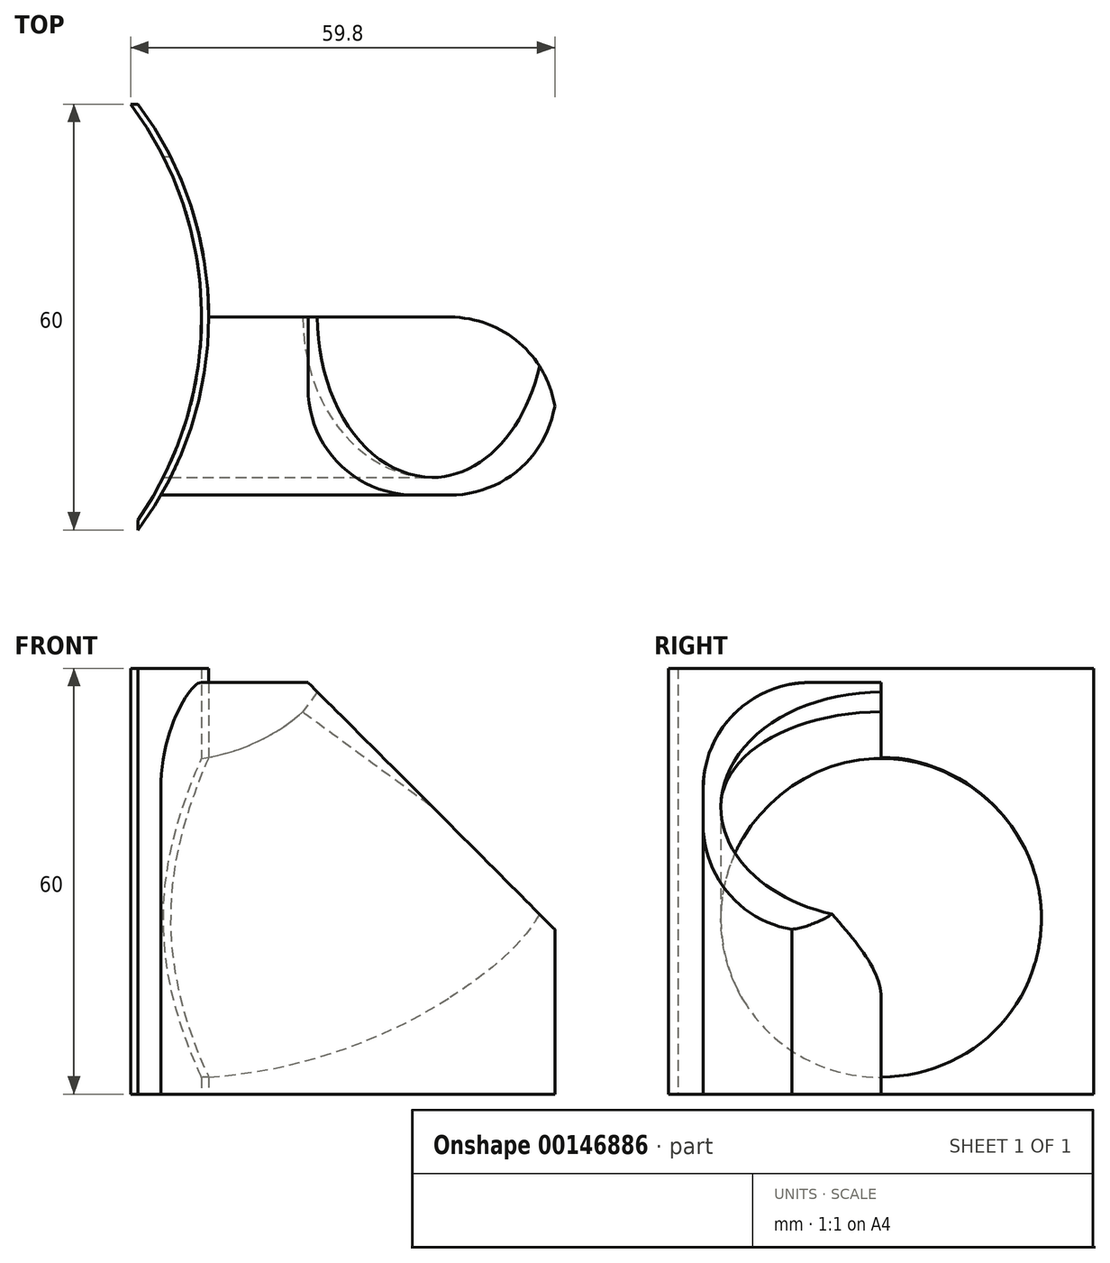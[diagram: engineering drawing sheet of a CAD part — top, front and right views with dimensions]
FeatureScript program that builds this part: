
annotation { "Feature Type Name" : "Feature", "Feature Type Description" : "" }
export const myFeature = defineFeature(function(context is Context, id is Id, definition is map)
    precondition{}
    {
        {
            var Q0;
            Q0=qCreatedBy(makeId("Top.planeOp"),FACE);
            var sketch = newSketch(context, id + "F0", { "sketchPlane" : qUnion([Q0])});
            skLineSegment(sketch, "E0.bottom", {"start": v(0, 0) * mm, "end": v(60, 0) * mm});
            skLineSegment(sketch, "E0.top", {"start": v(0, -60) * mm, "end": v(60, -60) * mm});
            skLineSegment(sketch, "E0.left", {"start": v(0, 0) * mm, "end": v(0, -60) * mm});
            skLineSegment(sketch, "E0.right", {"start": v(60, 0) * mm, "end": v(60, -60) * mm});
            skArc(sketch, "E1", {"start": v(0, -60) * mm, "mid": v(10, -30) * mm, "end": v(0, 0) * mm});
            skLineSegment(sketch, "E2.bottom", {"start": v(0, 0) * mm, "end": v(1, 0) * mm});
            skLineSegment(sketch, "E2.top", {"start": v(0, -60) * mm, "end": v(1, -60) * mm});
            skLineSegment(sketch, "E2.right", {"start": v(1, 0) * mm, "end": v(1, -60) * mm});
            skArc(sketch, "E3", {"start": v(1, -60) * mm, "mid": v(11, -30) * mm, "end": v(1, 0) * mm});
            skPoint(sketch, "E4", {"position": v(0, -30) * mm});
            skLineSegment(sketch, "E5.bottom", {"start": v(0, -30) * mm, "end": v(60, -30) * mm});
            skLineSegment(sketch, "E5.top", {"start": v(0, -4.9) * mm, "end": v(60, -4.9) * mm});
            skLineSegment(sketch, "E5.left", {"start": v(0, -30) * mm, "end": v(0, -4.9) * mm});
            skLineSegment(sketch, "E5.right", {"start": v(60, -30) * mm, "end": v(60, -4.9) * mm});
            skLineSegment(sketch, "E6.MirrorCS", {"start": v(0, -55.1) * mm, "end": v(60, -55.1) * mm});
            skSolve(sketch);
        }
        {
            var Q0;
            {var subQ0=sQuery(id+"F0.wireOp",EDGE,"E5.bottom");var subQ1=sQuery(id+"F0.wireOp",EDGE,"E1");var subQ2=makeQuery(id+"F0.imprint","INTERSECT",VERTEX,{"derivedFrom":[subQ1,subQ0]});Q0=makeQuery(id+"F0.imprint","IMPRINT",FACE,{"disambiguationData":[TD([[makeQuery(id+"F0.imprint","IMPRINT",EDGE,{"disambiguationData":[TD([[subQ2,-1.0]])],"derivedFrom":subQ1}),-1.0]])]});}
            var Q1;
            {var subQ0=sQuery(id+"F0.wireOp",EDGE,"E2.bottom");Q1=makeQuery(id+"F0.imprint","IMPRINT",FACE,{"disambiguationData":[TD([[makeQuery(id+"F0.imprint","IMPRINT",EDGE,{"derivedFrom":subQ0}),-1.0]])]});}
            var Q2;
            {var subQ0=sQuery(id+"F0.wireOp",EDGE,"E2.right");var subQ1=sQuery(id+"F0.wireOp",EDGE,"E1");var subQ2=makeQuery(id+"F0.imprint","INTERSECT",VERTEX,{"disambiguationData":[OD(1.0)],"derivedFrom":[subQ1,subQ0]});Q2=makeQuery(id+"F0.imprint","IMPRINT",FACE,{"disambiguationData":[TD([[makeQuery(id+"F0.imprint","IMPRINT",EDGE,{"disambiguationData":[TD([[subQ2,-1.0]])],"derivedFrom":subQ1}),-1.0]])]});}
            var Q3;
            {var subQ0=sQuery(id+"F0.wireOp",EDGE,"E6.MirrorCS");var subQ1=sQuery(id+"F0.wireOp",EDGE,"E1");var subQ2=makeQuery(id+"F0.imprint","INTERSECT",VERTEX,{"derivedFrom":[subQ1,subQ0]});Q3=makeQuery(id+"F0.imprint","IMPRINT",FACE,{"disambiguationData":[TD([[makeQuery(id+"F0.imprint","IMPRINT",EDGE,{"disambiguationData":[TD([[subQ2,-1.0]])],"derivedFrom":subQ1}),-1.0]])]});}
            var Q4;
            {var subQ1=sQuery(id+"F0.wireOp",EDGE,"E1");var subQ7=sQuery(id+"F0.wireOp",EDGE,"E2.right");var subQ8=makeQuery(id+"F0.imprint","INTERSECT",VERTEX,{"disambiguationData":[OD(0.0)],"derivedFrom":[subQ1,subQ7]});Q4=makeQuery(id+"F0.imprint","IMPRINT",FACE,{"disambiguationData":[TD([[makeQuery(id+"F0.imprint","IMPRINT",EDGE,{"disambiguationData":[TD([[subQ8,-1.0]])],"derivedFrom":subQ1}),-1.0]])]});}
            var Q5;
            {var subQ0=sQuery(id+"F0.wireOp",EDGE,"E2.top");Q5=makeQuery(id+"F0.imprint","IMPRINT",FACE,{"disambiguationData":[TD([[makeQuery(id+"F0.imprint","IMPRINT",EDGE,{"derivedFrom":subQ0}),1.0]])]});}
            var Q6;
            {var subQ0=sQuery(id+"F0.wireOp",EDGE,"E5.top");var subQ1=sQuery(id+"F0.wireOp",EDGE,"E1");var subQ2=makeQuery(id+"F0.imprint","INTERSECT",VERTEX,{"derivedFrom":[subQ1,subQ0]});Q6=makeQuery(id+"F0.imprint","IMPRINT",FACE,{"disambiguationData":[TD([[makeQuery(id+"F0.imprint","IMPRINT",EDGE,{"disambiguationData":[TD([[subQ2,-1.0]])],"derivedFrom":subQ1}),-1.0]])]});}
            extrude(context, id + "F1", {"entities" : qUnion([Q0, Q1, Q2, Q3, Q4, Q5, Q6]), "depth" : 60 * mm});
        }
        {
            var Q0;
            {var subQ5=sQuery(id+"F0.wireOp",EDGE,"E5.right");Q0=makeQuery(id+"F0.imprint","IMPRINT",FACE,{"disambiguationData":[TD([[makeQuery(id+"F0.imprint","IMPRINT",EDGE,{"derivedFrom":subQ5}),1.0]])]});}
            var Q1;
            {var subQ3=sQuery(id+"F0.wireOp",EDGE,"E6.MirrorCS");var subQ5=sQuery(id+"F0.wireOp",EDGE,"E3");var subQ6=makeQuery(id+"F0.imprint","INTERSECT",VERTEX,{"derivedFrom":[subQ5,subQ3]});Q1=makeQuery(id+"F0.imprint","IMPRINT",FACE,{"disambiguationData":[TD([[makeQuery(id+"F0.imprint","IMPRINT",EDGE,{"disambiguationData":[TD([[subQ6,-1.0]])],"derivedFrom":subQ5}),-1.0]])]});}
            extrude(context, id + "F2", {"entities" : qUnion([Q0, Q1]), "operationType" : NewBodyOperationType.ADD, "depth" : 58 * mm});
        }
        {
            var Q0;
            Q0=makeQuery(id+"F2.opExtrude","SWEPT_FACE",FACE,{"disambiguationData":[OSD([sQuery(id+"F0.wireOp",EDGE,"E6.MirrorCS")])]});
            var sketch = newSketch(context, id + "F3", { "sketchPlane" : qUnion([Q0])});
            skSolve(sketch);
        }
        {
            var Q0;
            {var subQ0=sQuery(id+"F0.wireOp",EDGE,"E6.MirrorCS");Q0=makeQuery(id+"F3.imprint","IMPRINT",FACE,{"disambiguationData":[TD([[makeQuery(id+"F3.imprint","IMPRINT",EDGE,{"derivedFrom":makeQuery(id+"F2.opExtrude","CAP_EDGE",EDGE,{"disambiguationData":[OSD([subQ0])],"isStart":true})}),1.0]])]});}
            var sketch = newSketch(context, id + "F4", { "sketchPlane" : qUnion([Q0])});
            skLineSegment(sketch, "E7.bottom", {"start": v(0, 0) * mm, "end": v(25, 0) * mm});
            skLineSegment(sketch, "E7.top", {"start": v(0, 58) * mm, "end": v(25, 58) * mm});
            skLineSegment(sketch, "E7.left", {"start": v(0, 0) * mm, "end": v(0, 58) * mm});
            skLineSegment(sketch, "E7.right", {"start": v(25, 0) * mm, "end": v(25, 58) * mm});
            skLineSegment(sketch, "E8.bottom", {"start": v(25, 0) * mm, "end": v(60, 0) * mm});
            skLineSegment(sketch, "E8.top", {"start": v(25, 23) * mm, "end": v(60, 23) * mm});
            skLineSegment(sketch, "E8.left", {"start": v(25, 0) * mm, "end": v(25, 23) * mm});
            skLineSegment(sketch, "E8.right", {"start": v(60, 0) * mm, "end": v(60, 23) * mm});
            skLineSegment(sketch, "E9", {"start": v(25, 58) * mm, "end": v(60, 23) * mm});
            skSolve(sketch);
        }
        {
            var Q0;
            {var subQ0=sQuery(id+"F4.wireOp",EDGE,"E9");Q0=makeQuery(id+"F4.imprint","IMPRINT",FACE,{"disambiguationData":[TD([[makeQuery(id+"F4.imprint","IMPRINT",EDGE,{"derivedFrom":subQ0}),1.0]])]});}
            extrude(context, id + "F5", {"entities" : qUnion([Q0]), "operationType" : NewBodyOperationType.REMOVE, "oppositeDirection" : true, "depth" : 60 * mm});
        }
        {
            var Q0;
            Q0=makeQuery(id+"F5.boolean.opBoolean","COPY",FACE,{"derivedFrom":makeQuery(id+"F5.opExtrude","SWEPT_FACE",FACE,{"disambiguationData":[OSD([sQuery(id+"F4.wireOp",EDGE,"E9")])]})});
            var sketch = newSketch(context, id + "F6", { "sketchPlane" : qUnion([Q0])});
            skLineSegment(sketch, "E10.bottom", {"start": v(26.16, -55.1) * mm, "end": v(1.41, -55.1) * mm});
            skLineSegment(sketch, "E10.top", {"start": v(26.16, -30) * mm, "end": v(1.41, -30) * mm});
            skLineSegment(sketch, "E10.left", {"start": v(26.16, -55.1) * mm, "end": v(26.16, -30) * mm});
            skLineSegment(sketch, "E10.right", {"start": v(1.41, -55.1) * mm, "end": v(1.41, -30) * mm});
            skCircle(sketch, "E11", {"center": v(1.41, -30) * mm, "radius": 22.6 * mm});
            skCircle(sketch, "E12", {"center": v(1.41, -30) * mm, "radius": 24.7 * mm});
            skLineSegment(sketch, "E13", {"start": v(1.41, -30) * mm, "end": v(1.41, -7.4) * mm});
            skLineSegment(sketch, "E14", {"start": v(1.41, -30) * mm, "end": v(-21.19, -30) * mm});
            skSolve(sketch);
        }
        {
            var Q0;
            Q0=qCreatedBy(makeId("Right.planeOp"),FACE);
            var sketch = newSketch(context, id + "F7", { "sketchPlane" : qUnion([Q0])});
            skLineSegment(sketch, "E15.bottom", {"start": v(0, 0) * mm, "end": v(-30, 0) * mm});
            skLineSegment(sketch, "E15.top", {"start": v(0, 25.1) * mm, "end": v(-30, 25.1) * mm});
            skLineSegment(sketch, "E15.left", {"start": v(0, 0) * mm, "end": v(0, 25.1) * mm});
            skLineSegment(sketch, "E15.right", {"start": v(-30, 0) * mm, "end": v(-30, 25.1) * mm});
            skCircle(sketch, "E16", {"center": v(-30, 25.1) * mm, "radius": 22.6 * mm});
            skSolve(sketch);
        }
        {
            var Q0;
            Q0=sQuery(id+"F7.wireOp",VERTEX,"E16.center");
            var Q1;
            Q1=qCreatedBy(makeId("Front.planeOp"),FACE);
            cPlane(context, id + "F8", {"entities" : qUnion([Q0, Q1]), "cplaneType" : CPlaneType.PLANE_POINT, "offset" : 25 * mm, "width" : 150 * mm, "height" : 150 * mm});
        }
        {
            var Q0;
            Q0=qCreatedBy(id+"F8.planeOp",FACE);
            var sketch = newSketch(context, id + "F9", { "sketchPlane" : qUnion([Q0])});
            skPoint(sketch, "E17", {"position": v(42.5, 40.5) * mm});
            skPoint(sketch, "E18", {"position": v(0, 25.1) * mm});
            skArc(sketch, "E19", {"start": v(0, 25.1) * mm, "mid": v(23.09, 27.72) * mm, "end": v(42.5, 40.5) * mm});
            skSolve(sketch);
        }
        {
            var Q0;
            {var subQ0=sQuery(id+"F7.wireOp",EDGE,"E15.right");var subQ1=sQuery(id+"F7.wireOp",EDGE,"E15.top");var subQ2=makeQuery(id+"F7.imprint","INTERSECT",VERTEX,{"derivedFrom":[subQ1,subQ0]});Q0=makeQuery(id+"F7.imprint","IMPRINT",FACE,{"disambiguationData":[TD([[makeQuery(id+"F7.imprint","IMPRINT",EDGE,{"disambiguationData":[TD([[subQ2,1.0]])],"derivedFrom":subQ1}),1.0]])]});}
            var Q1;
            {var subQ0=sQuery(id+"F7.wireOp",EDGE,"E15.right");var subQ1=sQuery(id+"F7.wireOp",EDGE,"E15.top");var subQ2=makeQuery(id+"F7.imprint","INTERSECT",VERTEX,{"derivedFrom":[subQ1,subQ0]});Q1=makeQuery(id+"F7.imprint","IMPRINT",FACE,{"disambiguationData":[TD([[makeQuery(id+"F7.imprint","IMPRINT",EDGE,{"disambiguationData":[TD([[subQ2,1.0]])],"derivedFrom":subQ1}),-1.0]])]});}
            var Q2;
            Q2=sQuery(id+"F9.wireOp",EDGE,"E19");
            sweep(context, id + "F10", {"operationType" : NewBodyOperationType.REMOVE, "profiles" : qUnion([Q0, Q1]), "path" : qUnion([Q2])});
        }
        {
            var Q0;
            Q0=makeQuery(id+"F10.boolean.opBoolean","COPY",FACE,{"derivedFrom":makeQuery(id+"F10.opSweep","CAP_FACE",FACE,{"disambiguationData":[OSD([sQuery(id+"F7.wireOp",EDGE,"E16"),sQuery(id+"F9.wireOp",VERTEX,"E19.end")])],"isStart":false})});
            extrude(context, id + "F11", {"entities" : qUnion([Q0]), "operationType" : NewBodyOperationType.REMOVE, "oppositeDirection" : true, "depth" : 25 * mm});
        }
        {
            var Q0;
            Q0=makeQuery(id+"F2.opExtrude","CAP_EDGE",EDGE,{"disambiguationData":[OSD([sQuery(id+"F0.wireOp",EDGE,"E6.MirrorCS")])],"isStart":false});
            var Q1;
            Q1=makeQuery(id+"F2.opExtrude","CAP_EDGE",EDGE,{"disambiguationData":[OSD([sQuery(id+"F0.wireOp",EDGE,"E5.top")])],"isStart":false});
            var Q2;
            Q2=makeQuery(id+"F2.opExtrude","SWEPT_EDGE",EDGE,{"disambiguationData":[OSD([sQuery(id+"F0.wireOp",EDGE,"E0.right"),sQuery(id+"F0.wireOp",EDGE,"E6.MirrorCS")])]});
            var Q3;
            Q3=makeQuery(id+"F2.opExtrude","SWEPT_EDGE",EDGE,{"disambiguationData":[OSD([sQuery(id+"F0.wireOp",EDGE,"E0.right"),sQuery(id+"F0.wireOp",EDGE,"E5.top"),sQuery(id+"F0.wireOp",EDGE,"E5.right")])]});
            fillet(context, id + "F12", {"entities" : qUnion([Q0, Q1, Q2, Q3]), "radius" : 15 * mm, "tangentPropagation" : true, "allowEdgeOverflow" : false});
        }
    });
